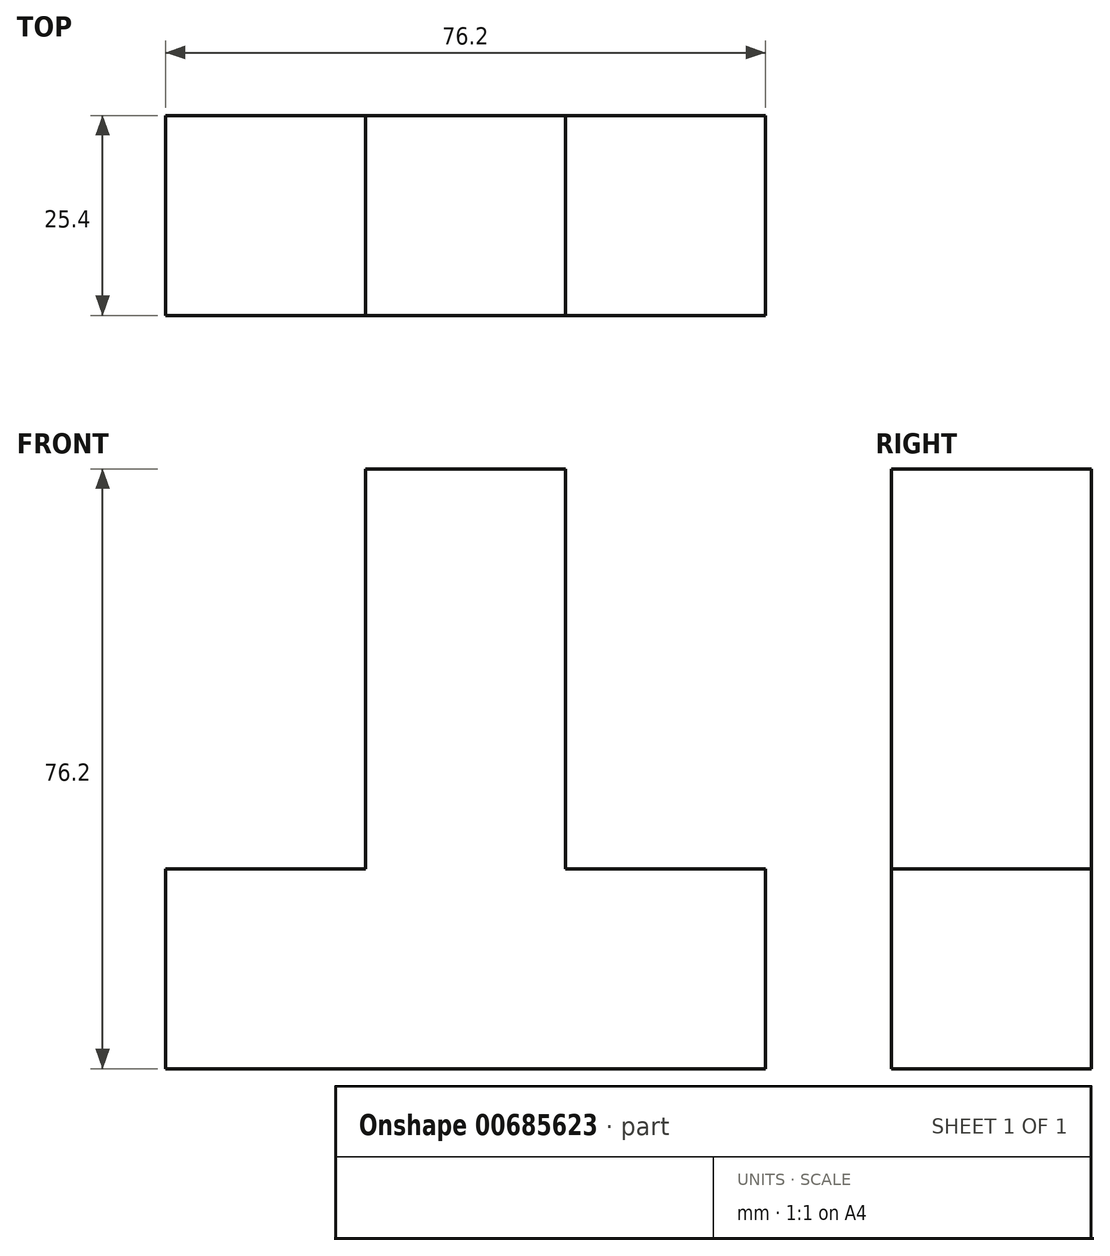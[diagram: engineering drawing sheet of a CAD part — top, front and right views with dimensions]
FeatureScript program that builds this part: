
annotation { "Feature Type Name" : "Feature", "Feature Type Description" : "" }
export const myFeature = defineFeature(function(context is Context, id is Id, definition is map)
    precondition{}
    {
        {
            var Q0;
            Q0=qCreatedBy(makeId("Front.planeOp"),FACE);
            var sketch = newSketch(context, id + "F0", { "sketchPlane" : qUnion([Q0])});
            skLineSegment(sketch, "E0", {"start": v(-74.96, 25.4) * mm, "end": v(-74.96, 0) * mm});
            skLineSegment(sketch, "E1", {"start": v(-74.96, 0) * mm, "end": v(1.24, 0) * mm});
            skLineSegment(sketch, "E2", {"start": v(1.24, 0) * mm, "end": v(1.24, 25.4) * mm});
            skLineSegment(sketch, "E3", {"start": v(-74.96, 25.4) * mm, "end": v(-49.56, 25.4) * mm});
            skLineSegment(sketch, "E4", {"start": v(-49.56, 25.4) * mm, "end": v(-49.56, 76.2) * mm});
            skLineSegment(sketch, "E5", {"start": v(-49.56, 76.2) * mm, "end": v(-24.16, 76.2) * mm});
            skLineSegment(sketch, "E6", {"start": v(-24.16, 76.2) * mm, "end": v(-24.16, 25.4) * mm});
            skLineSegment(sketch, "E7", {"start": v(-24.16, 25.4) * mm, "end": v(1.24, 25.4) * mm});
            skSolve(sketch);
        }
        {
            var Q0;
            Q0=makeQuery(id+"F0.imprint","IMPRINT",FACE,{"disambiguationData":[TD([[makeQuery(id+"F0.imprint","IMPRINT",EDGE,{"derivedFrom":sQuery(id+"F0.wireOp",EDGE,"E0")}),1.0]])]});
            extrude(context, id + "F1", {"entities" : qUnion([Q0]), "depth" : 25.4 * mm, "offsetDistance" : 25.4 * mm});
        }
    });
